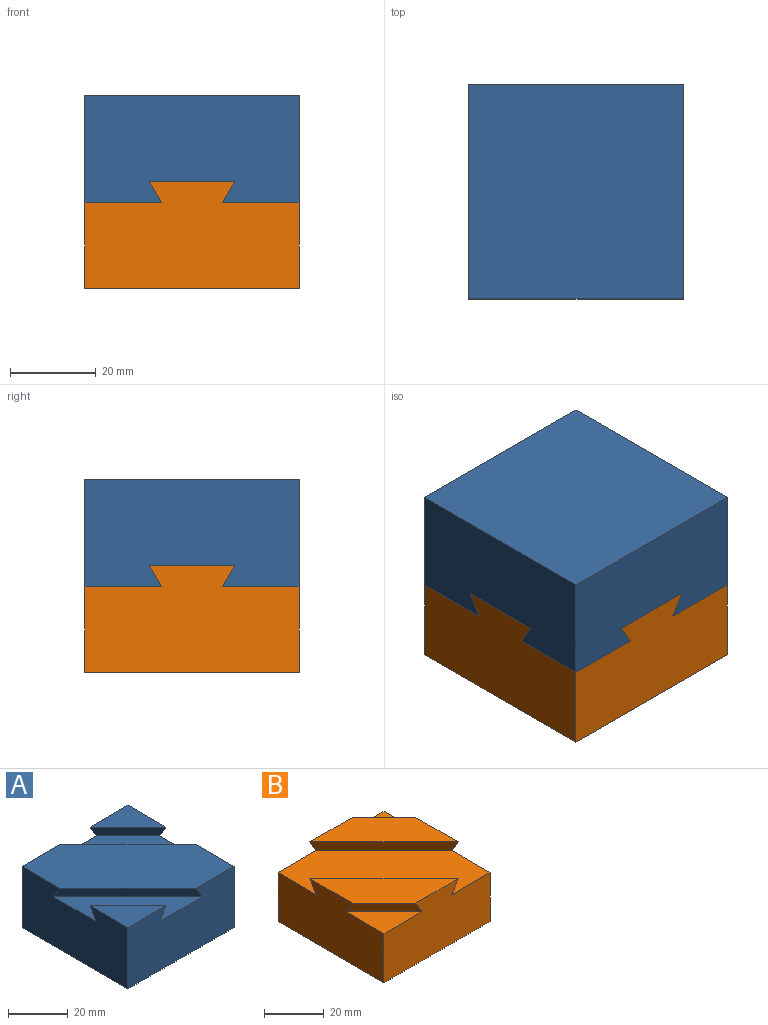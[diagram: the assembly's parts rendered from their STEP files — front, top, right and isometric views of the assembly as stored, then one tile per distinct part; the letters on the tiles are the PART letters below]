
ASSEMBLY  parts=2 mates=1
PART A: 14 faces, bbox 50x50x25 mm
  f0: plane 17.89x17.89mm, normal (0,0,1), area 160mm2, adj f1,f5,f12
  f1: plane 50x25mm, normal (1,0,0), area 1164.4mm2, adj f0,f2,f4,f5,f7,f11,f12,f13
  f2: plane 50x50mm, normal (0,0,1), area 1468.7mm2, adj f1,f3,f4,f5,f9,f13
  f3: plane 50x25mm, normal (-1,0,0), area 1164.4mm2, adj f2,f4,f5,f6,f7,f8,f9,f10
  f4: plane 50x25mm, normal (0,-1,0), area 1164.4mm2, adj f1,f2,f3,f6,f7,f8,f9,f10
  f5: plane 50x25mm, normal (0,1,0), area 1164.4mm2, adj f0,f1,f2,f3,f7,f11,f12,f13
  f6: plane 17.89x17.89mm, normal (0,0,1), area 160mm2, adj f3,f4,f10
  f7: plane 50x50mm, normal (0,0,-1), area 2500mm2, adj f1,f3,f4,f5
  f8: plane 35x35mm, normal (0,0,1), area 500mm2, adj f3,f4,f9,f10
  f9: plane 35x35mm, normal (-0.65,-0.65,-0.38), area 256.3mm2, adj f2,f3,f4,f8
  f10: plane 17.89x17.89mm, normal (0.65,0.65,-0.38), area 125.6mm2, adj f3,f4,f6,f8
  f11: plane 35x35mm, normal (0,0,1), area 500mm2, adj f1,f5,f12,f13
  f12: plane 17.89x17.89mm, normal (-0.65,-0.65,-0.38), area 125.6mm2, adj f0,f1,f5,f11
  f13: plane 35x35mm, normal (0.65,0.65,-0.38), area 256.3mm2, adj f1,f2,f5,f11
PART B: 14 faces, bbox 50x50x25 mm
  f0: plane 35x35mm, normal (0,0,1), area 500mm2, adj f1,f2,f11,f13
  f1: plane 50x25mm, normal (0,1,0), area 1085.6mm2, adj f0,f2,f3,f6,f10,f11,f12,f13
  f2: plane 50x25mm, normal (1,0,0), area 1085.6mm2, adj f0,f1,f4,f6,f10,f11,f12,f13
  f3: plane 50x25mm, normal (-1,0,0), area 1085.6mm2, adj f1,f4,f5,f6,f7,f8,f9,f10
  f4: plane 50x25mm, normal (0,-1,0), area 1085.6mm2, adj f2,f3,f5,f6,f7,f8,f9,f10
  f5: plane 35x35mm, normal (0,0,1), area 500mm2, adj f3,f4,f7,f9
  f6: plane 50x50mm, normal (0,0,-1), area 2500mm2, adj f1,f2,f3,f4
  f7: plane 17.89x17.89mm, normal (-0.65,-0.65,-0.38), area 125.6mm2, adj f3,f4,f5,f8
  f8: plane 17.89x17.89mm, normal (0,0,1), area 160mm2, adj f3,f4,f7
  f9: plane 35x35mm, normal (0.65,0.65,-0.38), area 256.3mm2, adj f3,f4,f5,f10
  f10: plane 50x50mm, normal (0,0,1), area 1468.7mm2, adj f1,f2,f3,f4,f9,f11
  f11: plane 35x35mm, normal (-0.65,-0.65,-0.38), area 256.3mm2, adj f0,f1,f2,f10
  f12: plane 17.89x17.89mm, normal (0,0,1), area 160mm2, adj f1,f2,f13
  f13: plane 17.89x17.89mm, normal (0.65,0.65,-0.38), area 125.6mm2, adj f0,f1,f2,f12
PLACE A rot(axis=(-0.71,-0.71,0),180deg) t=(-60.55,-135.52,4.15)mm
PLACE B t=(-60.55,-135.52,-40.85)mm
MATE parallel B.f10 <-> A.f2  axis (0,0,1) through (-60.55,-135.52,-20.85)mm
